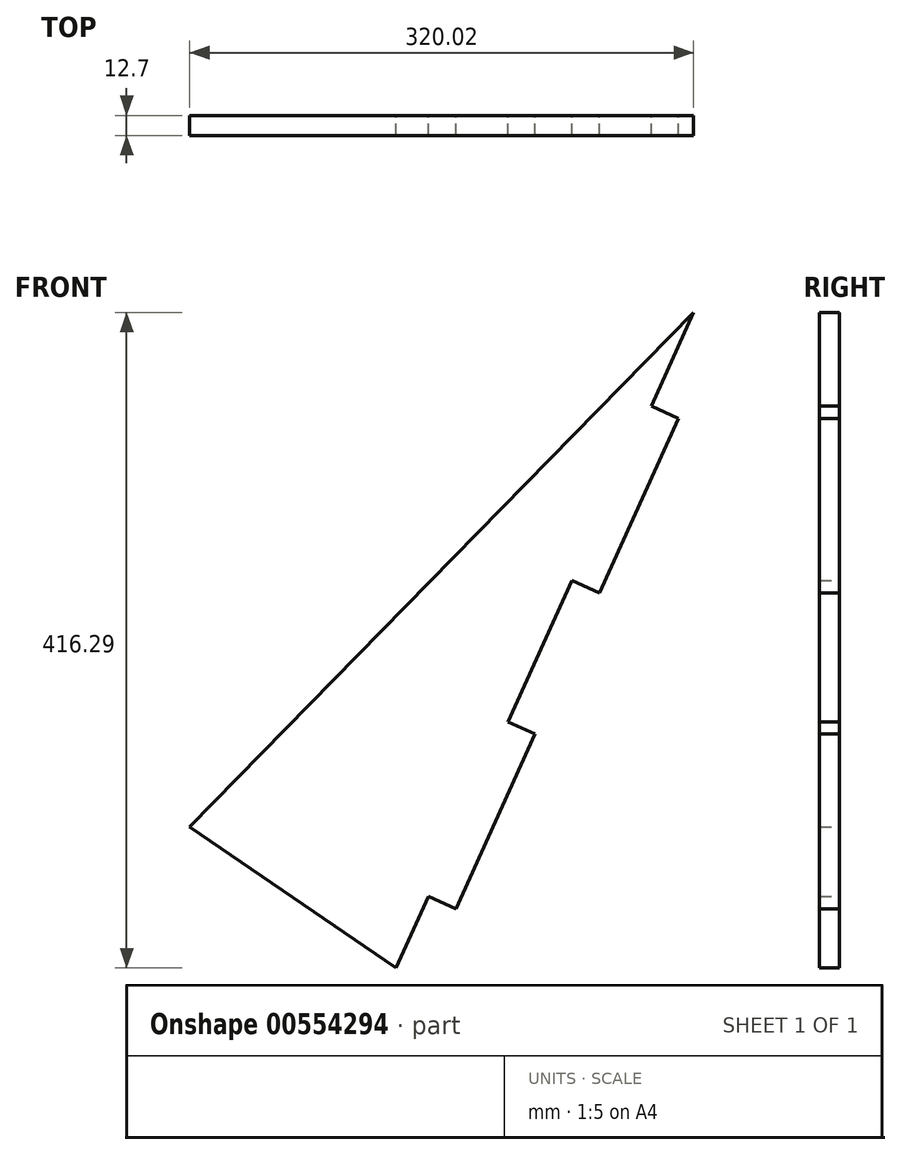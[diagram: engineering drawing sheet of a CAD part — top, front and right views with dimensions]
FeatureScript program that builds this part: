
annotation { "Feature Type Name" : "Feature", "Feature Type Description" : "" }
export const myFeature = defineFeature(function(context is Context, id is Id, definition is map)
    precondition{}
    {
        {
            var Q0;
            Q0=qCreatedBy(makeId("Front.planeOp"),FACE);
            var sketch = newSketch(context, id + "F0", { "sketchPlane" : qUnion([Q0])});
            skLineSegment(sketch, "E0", {"start": v(-320.02, 0) * mm, "end": v(0, 326.53) * mm});
            skLineSegment(sketch, "E1", {"start": v(-320.02, 0) * mm, "end": v(-189.04, -89.76) * mm});
            skLineSegment(sketch, "E2", {"start": v(-189.04, -89.76) * mm, "end": v(0, 326.53) * mm});
            skSolve(sketch);
        }
        {
            var Q0;
            Q0=makeQuery(id+"F0.imprint","IMPRINT",FACE,{"disambiguationData":[TD([[makeQuery(id+"F0.imprint","IMPRINT",EDGE,{"derivedFrom":sQuery(id+"F0.wireOp",EDGE,"E0")}),-1.0]])]});
            extrude(context, id + "F1", {"entities" : qUnion([Q0]), "depth" : 12.7 * mm, "offsetDistance" : 30.48 * mm});
        }
        {
            var Q0;
            Q0=makeQuery(id+"F1.opExtrude","SWEPT_FACE",FACE,{"disambiguationData":[OSD([sQuery(id+"F0.wireOp",EDGE,"E2")])]});
            var sketch = newSketch(context, id + "F2", { "sketchPlane" : qUnion([Q0])});
            skLineSegment(sketch, "E3.bottom", {"start": v(-12.7, 232.22) * mm, "end": v(0, 232.22) * mm});
            skLineSegment(sketch, "E3.top", {"start": v(-12.7, 110.3) * mm, "end": v(0, 110.3) * mm});
            skLineSegment(sketch, "E3.left", {"start": v(-12.7, 232.22) * mm, "end": v(-12.7, 110.3) * mm});
            skLineSegment(sketch, "E3.right", {"start": v(0, 232.22) * mm, "end": v(0, 110.3) * mm});
            skLineSegment(sketch, "E4.bottom", {"start": v(-12.7, 11.94) * mm, "end": v(0, 11.94) * mm});
            skLineSegment(sketch, "E4.top", {"start": v(-12.7, -109.98) * mm, "end": v(0, -109.98) * mm});
            skLineSegment(sketch, "E4.left", {"start": v(-12.7, 11.94) * mm, "end": v(-12.7, -109.98) * mm});
            skLineSegment(sketch, "E4.right", {"start": v(0, 11.94) * mm, "end": v(0, -109.98) * mm});
            skSolve(sketch);
        }
        {
            var Q0;
            Q0 = qSketchRegion(id + "F2", true);
            extrude(context, id + "F3", {"entities" : qUnion([Q0]), "operationType" : NewBodyOperationType.ADD, "depth" : 19.05 * mm, "offsetDistance" : 30.48 * mm});
        }
    });
